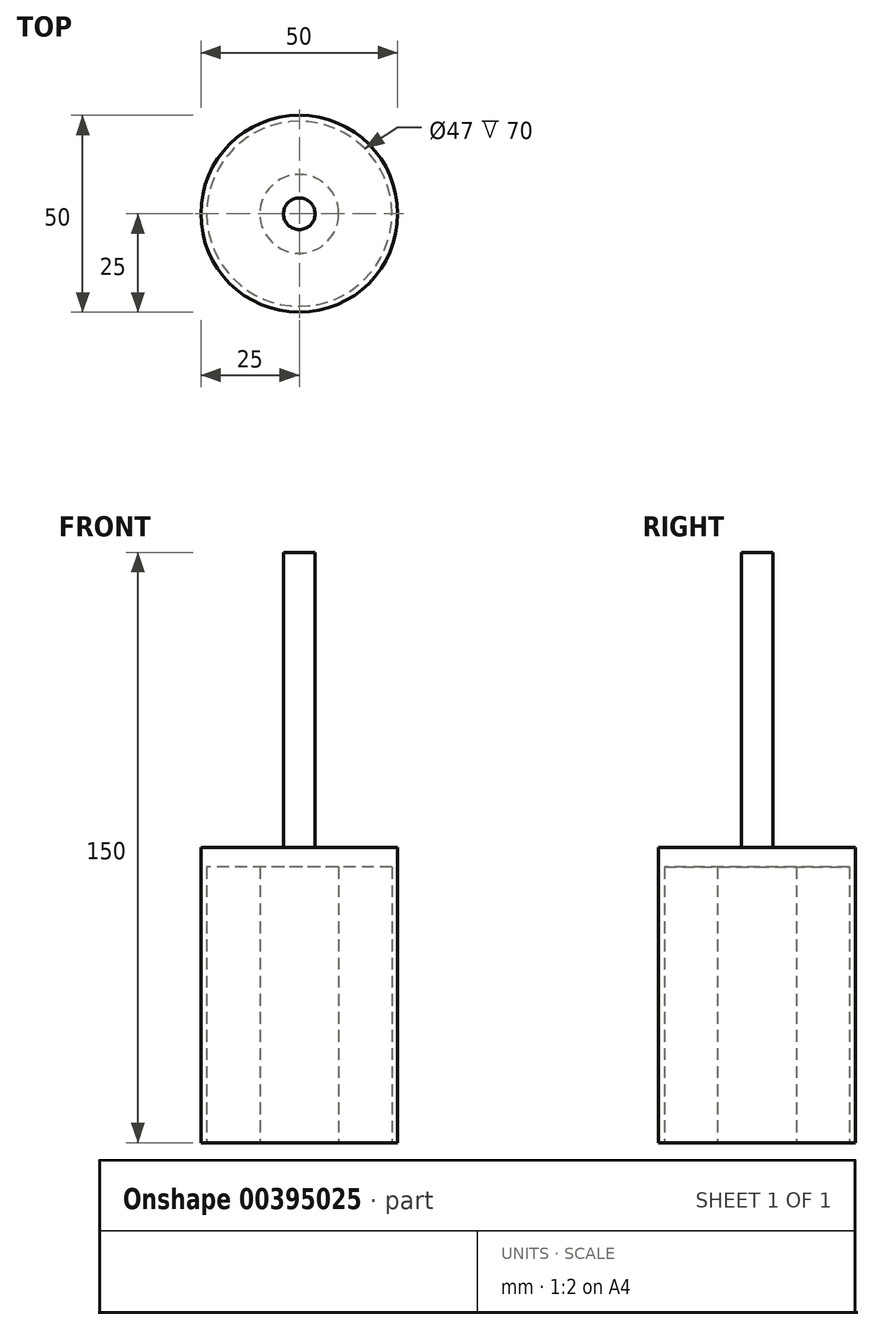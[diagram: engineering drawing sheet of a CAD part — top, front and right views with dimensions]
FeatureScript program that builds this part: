
annotation { "Feature Type Name" : "Feature", "Feature Type Description" : "" }
export const myFeature = defineFeature(function(context is Context, id is Id, definition is map)
    precondition{}
    {
        {
            var Q0;
            Q0=qCreatedBy(makeId("Top.planeOp"),FACE);
            var sketch = newSketch(context, id + "F0", { "sketchPlane" : qUnion([Q0])});
            skCircle(sketch, "E0", {"center": v(0, 0) * mm, "radius": 25 * mm});
            skCircle(sketch, "E1", {"center": v(0, 0) * mm, "radius": 23.5 * mm});
            skCircle(sketch, "E2", {"center": v(0, 0) * mm, "radius": 10 * mm});
            skSolve(sketch);
        }
        {
            var Q0;
            Q0=makeQuery(id+"F0.imprint","IMPRINT",FACE,{"disambiguationData":[TD([[makeQuery(id+"F0.imprint","IMPRINT",EDGE,{"derivedFrom":sQuery(id+"F0.wireOp",EDGE,"E0")}),1.0]])]});
            extrude(context, id + "F1", {"entities" : qUnion([Q0]), "depth" : 70 * mm});
        }
        {
            var Q0;
            Q0=makeQuery(id+"F1.opExtrude","CAP_FACE",FACE,{"disambiguationData":[OSD([sQuery(id+"F0.wireOp",EDGE,"E0"),sQuery(id+"F0.wireOp",EDGE,"E1")])],"isStart":false});
            var sketch = newSketch(context, id + "F2", { "sketchPlane" : qUnion([Q0])});
            skCircle(sketch, "E3", {"center": v(0, 0) * mm, "radius": 25 * mm});
            skSolve(sketch);
        }
        {
            var Q0;
            Q0 = qSketchRegion(id + "F2", true);
            extrude(context, id + "F3", {"entities" : qUnion([Q0]), "operationType" : NewBodyOperationType.ADD, "depth" : 5 * mm});
        }
        {
            var Q0;
            Q0=makeQuery(id+"F3.opExtrude","CAP_FACE",FACE,{"disambiguationData":[OSD([sQuery(id+"F2.wireOp",EDGE,"E3")])],"isStart":false});
            var sketch = newSketch(context, id + "F4", { "sketchPlane" : qUnion([Q0])});
            skCircle(sketch, "E4", {"center": v(0, 0) * mm, "radius": 4 * mm});
            skSolve(sketch);
        }
        {
            var Q0;
            Q0=makeQuery(id+"F4.imprint","IMPRINT",FACE,{"disambiguationData":[TD([[makeQuery(id+"F4.imprint","IMPRINT",EDGE,{"derivedFrom":sQuery(id+"F4.wireOp",EDGE,"E4")}),1.0]])]});
            extrude(context, id + "F5", {"entities" : qUnion([Q0]), "operationType" : NewBodyOperationType.ADD, "depth" : 75 * mm});
        }
        {
            var Q0;
            Q0=makeQuery(id+"F0.imprint","IMPRINT",FACE,{"disambiguationData":[TD([[makeQuery(id+"F0.imprint","IMPRINT",EDGE,{"derivedFrom":sQuery(id+"F0.wireOp",EDGE,"E2")}),1.0]])]});
            extrude(context, id + "F6", {"entities" : qUnion([Q0]), "operationType" : NewBodyOperationType.ADD, "depth" : 75 * mm});
        }
    });
